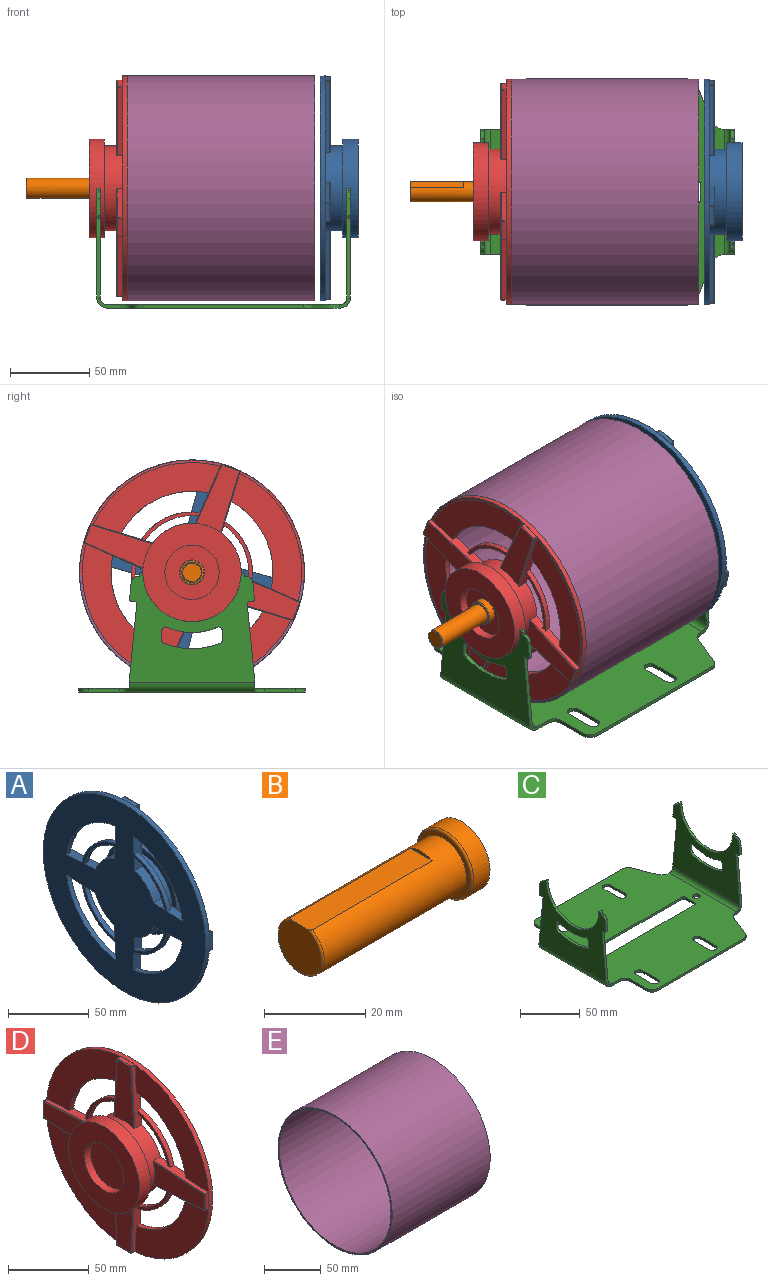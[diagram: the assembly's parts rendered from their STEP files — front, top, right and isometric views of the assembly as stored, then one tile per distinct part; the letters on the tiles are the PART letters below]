
ASSEMBLY  parts=5 mates=4
PART A: 69 faces, bbox 24x142.2x142.2 mm
  f0: plane 34.29x34.29mm, normal (1,0,0), area 923.5mm2, adj f5
  f1: cylinder r=26.92mm len=53.85mm, axis (1,0,0), area 1960.8mm2, adj f2,f6,f7,f8,f9,f10,f11,f12
  f2: plane 62.23x62.23mm, normal (-1,0,0), area 764.2mm2, adj f1,f3
  f3: cylinder r=31.12mm len=62.23mm, axis (1,0,0), area 1862.1mm2, adj f2,f4
  f4: plane 62.23x62.23mm, normal (1,0,0), area 2118mm2, adj f3,f5
  f5: cylinder r=17.14mm len=34.29mm, axis (1,0,0), area 574.6mm2, adj f0,f4
  f6: plane 142.24x142.24mm, normal (-1,0,0), area 11924.2mm2, adj f1,f15,f16,f17,f19,f20,f33,f34
  f7: cylinder r=0.51mm len=45.04mm, axis (0,0.06,1), area 35.9mm2, adj f1,f33,f53,f54
  f8: cylinder r=0.51mm len=45.04mm, axis (0,0.06,-1), area 35.9mm2, adj f1,f34,f53,f56
  f9: cylinder r=0.51mm len=45.04mm, axis (0,-1,0.06), area 35.9mm2, adj f1,f35,f57,f58
  f10: cylinder r=0.51mm len=45.04mm, axis (0,1,0.06), area 35.9mm2, adj f1,f36,f57,f60
  f11: cylinder r=0.51mm len=45.04mm, axis (0,-0.06,-1), area 35.9mm2, adj f1,f37,f61,f62
  f12: cylinder r=0.51mm len=45.04mm, axis (0,-0.06,1), area 35.9mm2, adj f1,f38,f61,f64
  f13: cylinder r=0.51mm len=45.04mm, axis (0,1,-0.06), area 35.9mm2, adj f1,f39,f65,f66
  f14: cylinder r=0.51mm len=45.04mm, axis (0,-1,-0.06), area 35.9mm2, adj f1,f40,f65,f68
  f15: cylinder r=51.26mm len=43.12mm, axis (1,0,0), area 215.7mm2, adj f6,f18,f33,f36
  f16: cylinder r=51.26mm len=43.12mm, axis (1,0,0), area 215.7mm2, adj f6,f18,f35,f38
  f17: cylinder r=51.26mm len=43.12mm, axis (1,0,0), area 215.7mm2, adj f6,f18,f37,f40
  f18: plane 142.24x142.24mm, normal (1,0,0), area 6535.9mm2, adj f15,f16,f17,f19,f20,f21,f22,f23
  f19: cylinder r=71.12mm len=142.24mm, axis (1,0,0), area 1475.5mm2, adj f6,f18
  f20: cylinder r=51.26mm len=43.12mm, axis (1,0,0), area 215.7mm2, adj f6,f18,f34,f39
  f21: plane 11.8x2.79mm, normal (0,0,1), area 33mm2, adj f18,f22,f23,f55
  f22: cylinder r=0.51mm len=2.79mm, axis (-1,0,0), area 2.1mm2, adj f18,f21,f33,f54
  f23: cylinder r=0.51mm len=2.79mm, axis (-1,0,0), area 2.1mm2, adj f18,f21,f34,f56
  f24: plane 11.8x2.79mm, normal (0,-1,0), area 33mm2, adj f18,f25,f26,f59
  f25: cylinder r=0.51mm len=2.79mm, axis (-1,0,0), area 2.1mm2, adj f18,f24,f35,f58
  f26: cylinder r=0.51mm len=2.79mm, axis (-1,0,0), area 2.1mm2, adj f18,f24,f36,f60
  f27: plane 11.8x2.79mm, normal (0,0,-1), area 33mm2, adj f18,f28,f29,f63
  f28: cylinder r=0.51mm len=2.79mm, axis (-1,0,0), area 2.1mm2, adj f18,f27,f37,f62
  f29: cylinder r=0.51mm len=2.79mm, axis (-1,0,0), area 2.1mm2, adj f18,f27,f38,f64
  f30: plane 11.8x2.79mm, normal (0,1,0), area 33mm2, adj f18,f31,f32,f67
  f31: cylinder r=0.51mm len=2.79mm, axis (-1,0,0), area 2.1mm2, adj f18,f30,f39,f66
  f32: cylinder r=0.51mm len=2.79mm, axis (-1,0,0), area 2.1mm2, adj f18,f30,f40,f68
  f33: plane 45.01x6.1mm, normal (0,-1,0.06), area 201.9mm2, adj f1,f6,f7,f15,f18,f22,f50,f51
  f34: plane 45.01x6.1mm, normal (0,1,0.06), area 201.9mm2, adj f1,f6,f8,f18,f20,f23,f41,f42
  f35: plane 45.01x6.1mm, normal (0,-0.06,-1), area 201.9mm2, adj f1,f6,f9,f16,f18,f25,f47,f48
  f36: plane 45.01x6.1mm, normal (0,-0.06,1), area 201.9mm2, adj f1,f6,f10,f15,f18,f26,f50,f51
  f37: plane 45.01x6.1mm, normal (0,1,-0.06), area 201.9mm2, adj f1,f6,f11,f17,f18,f28,f44,f45
  f38: plane 45.01x6.1mm, normal (0,-1,-0.06), area 201.9mm2, adj f1,f6,f12,f16,f18,f29,f47,f48
  f39: plane 45.01x6.1mm, normal (0,0.06,1), area 201.9mm2, adj f1,f6,f13,f18,f20,f31,f41,f42
  f40: plane 45.01x6.1mm, normal (0,0.06,-1), area 201.9mm2, adj f1,f6,f14,f17,f18,f32,f44,f45
  f41: cylinder r=38.23mm len=28.94mm, axis (1,0,0), area 142.6mm2, adj f6,f34,f39,f43
  f42: cylinder r=35.94mm len=26.42mm, axis (1,0,0), area 129.7mm2, adj f6,f34,f39,f43
  f43: plane 28.94x28.94mm, normal (1,0,0), area 94.3mm2, adj f34,f39,f41,f42
  f44: cylinder r=38.23mm len=28.94mm, axis (1,0,0), area 142.6mm2, adj f6,f37,f40,f46
  f45: cylinder r=35.94mm len=26.42mm, axis (1,0,0), area 129.7mm2, adj f6,f37,f40,f46
  f46: plane 28.94x28.94mm, normal (1,0,0), area 94.3mm2, adj f37,f40,f44,f45
  f47: cylinder r=38.23mm len=28.94mm, axis (1,0,0), area 142.6mm2, adj f6,f35,f38,f49
  f48: cylinder r=35.94mm len=26.42mm, axis (1,0,0), area 129.7mm2, adj f6,f35,f38,f49
  f49: plane 28.94x28.94mm, normal (1,0,0), area 94.3mm2, adj f35,f38,f47,f48
  f50: cylinder r=38.23mm len=28.94mm, axis (1,0,0), area 142.6mm2, adj f6,f33,f36,f52
  f51: cylinder r=35.94mm len=26.42mm, axis (1,0,0), area 129.7mm2, adj f6,f33,f36,f52
  f52: plane 28.94x28.94mm, normal (1,0,0), area 94.3mm2, adj f33,f36,f50,f51
  f53: plane 44.8x17.1mm, normal (1,0,0), area 631.4mm2, adj f1,f7,f8,f55
  f54: sphere r=0.51mm, area 0.4mm2, adj f7,f22,f55
  f55: cylinder r=0.51mm len=11.8mm, axis (0,1,0), area 9.4mm2, adj f21,f53,f54,f56
  f56: sphere r=0.51mm, area 0.4mm2, adj f8,f23,f55
  f57: plane 44.8x17.1mm, normal (1,0,0), area 631.4mm2, adj f1,f9,f10,f59
  f58: sphere r=0.51mm, area 0.4mm2, adj f9,f25,f59
  f59: cylinder r=0.51mm len=11.8mm, axis (0,0,1), area 9.4mm2, adj f24,f57,f58,f60
  f60: sphere r=0.51mm, area 0.4mm2, adj f10,f26,f59
  f61: plane 44.8x17.1mm, normal (1,0,0), area 631.4mm2, adj f1,f11,f12,f63
  f62: sphere r=0.51mm, area 0.4mm2, adj f11,f28,f63
  f63: cylinder r=0.51mm len=11.8mm, axis (0,-1,0), area 9.4mm2, adj f27,f61,f62,f64
  f64: sphere r=0.51mm, area 0.4mm2, adj f12,f29,f63
  f65: plane 44.8x17.1mm, normal (1,0,0), area 631.4mm2, adj f1,f13,f14,f67
  f66: sphere r=0.51mm, area 0.4mm2, adj f13,f31,f67
  f67: cylinder r=0.51mm len=11.8mm, axis (0,0,-1), area 9.4mm2, adj f30,f65,f66,f68
  f68: sphere r=0.51mm, area 0.4mm2, adj f14,f32,f67
PART B: 9 faces, bbox 45.4x17.1x17.1 mm
  f0: plane 11.68x11.43mm, normal (-1,0,0), area 106.6mm2, adj f5,f7
  f1: cylinder r=7.89mm len=15.77mm, axis (1,0,0), area 226.6mm2, adj f2,f6
  f2: torus R=7.38mm, axis (1,0,0), area 38.6mm2, adj f1,f3
  f3: plane 14.76x14.76mm, normal (-1,0,0), area 44.4mm2, adj f2,f4
  f4: cylinder r=6.35mm len=39.78mm, axis (1,0,0), area 1376.3mm2, adj f3,f5,f7,f8
  f5: torus R=5.84mm, axis (1,0,0), area 26.7mm2, adj f0,f4,f7
  f6: plane 15.77x15.77mm, normal (1,0,0), area 195.4mm2, adj f1
  f7: plane 34.04x6.03mm, normal (0,0,1), area 205.1mm2, adj f0,f4,f5,f8
  f8: plane 6.03x0.76mm, normal (-1,0,0), area 3.1mm2, adj f4,f7
PART C: 108 faces, bbox 160.4x143x75.7 mm
  f0: plane 147.7x143mm, normal (0,0,-1), area 16724.9mm2, adj f2,f3,f12,f13,f14,f15,f18,f19
  f1: plane 147.7x143mm, normal (0,0,1), area 16724.9mm2, adj f2,f3,f12,f13,f16,f17,f18,f19
  f2: plane 6.64x6.35mm, normal (0,-1,0), area 19.4mm2, adj f0,f1,f15,f16,f45,f57
  f3: plane 6.64x6.35mm, normal (0,1,0), area 19.4mm2, adj f0,f1,f15,f16,f31,f72
  f4: plane 79.5x69.34mm, normal (1,0,0), area 3277.4mm2, adj f5,f6,f17,f73,f74,f75,f76,f77
  f5: plane 2.29x0.75mm, normal (0,0,1), area 1.7mm2, adj f4,f7,f96,f97
  f6: plane 2.29x0.75mm, normal (0,0,1), area 1.7mm2, adj f4,f7,f81,f97
  f7: plane 79.5x69.34mm, normal (-1,0,0), area 3277.4mm2, adj f5,f6,f14,f73,f74,f75,f76,f77
  f8: plane 79.5x69.34mm, normal (1,0,0), area 3277.4mm2, adj f9,f10,f15,f48,f49,f50,f51,f52
  f9: plane 2.29x0.75mm, normal (0,0,1), area 1.7mm2, adj f8,f11,f48,f65
  f10: plane 2.29x0.75mm, normal (0,0,1), area 1.7mm2, adj f8,f11,f48,f64
  f11: plane 79.5x69.34mm, normal (-1,0,0), area 3277.4mm2, adj f9,f10,f16,f48,f49,f50,f51,f52
  f12: plane 15.88x6.35mm, normal (0,-1,0), area 40.5mm2, adj f0,f1,f14,f17,f39,f88
  f13: plane 15.88x6.35mm, normal (0,1,0), area 40.5mm2, adj f0,f1,f14,f17,f32,f89
  f14: cylinder r=6.35mm len=79.5mm, axis (0,1,0), area 793mm2, adj f0,f7,f12,f13
  f15: cylinder r=6.35mm len=79.5mm, axis (0,1,0), area 793mm2, adj f0,f2,f3,f8
  f16: cylinder r=4.06mm len=79.5mm, axis (0,1,0), area 507.5mm2, adj f1,f2,f3,f11
  f17: cylinder r=4.06mm len=79.5mm, axis (0,1,0), area 507.5mm2, adj f1,f4,f12,f13
  f18: plane 22.07x8.65mm, normal (0.93,0.36,0), area 54.2mm2, adj f0,f1,f19,f31
  f19: cylinder r=6.35mm len=5.91mm, axis (0,0,-1), area 17.4mm2, adj f0,f1,f18,f20
  f20: plane 102.35x2.29mm, normal (0,1,0), area 234mm2, adj f0,f1,f19,f21
  f21: cylinder r=6.35mm len=6.35mm, axis (0,0,-1), area 22.8mm2, adj f0,f1,f20,f22
  f22: plane 19.05x2.29mm, normal (-1,0,0), area 43.5mm2, adj f0,f1,f21,f32
  f23: cylinder r=3.97mm len=7.94mm, axis (0,0,-1), area 28.5mm2, adj f0,f1,f24,f26
  f24: plane 17.46x2.29mm, normal (-1,0,0), area 39.9mm2, adj f0,f1,f23,f25
  f25: cylinder r=3.97mm len=7.94mm, axis (0,0,-1), area 28.5mm2, adj f0,f1,f24,f26
  f26: plane 17.46x2.29mm, normal (1,0,0), area 39.9mm2, adj f0,f1,f23,f25
  f27: plane 17.46x2.29mm, normal (1,0,0), area 39.9mm2, adj f0,f1,f28,f30
  f28: cylinder r=3.97mm len=7.94mm, axis (0,0,-1), area 28.5mm2, adj f0,f1,f27,f29
  f29: plane 17.46x2.29mm, normal (-1,0,0), area 39.9mm2, adj f0,f1,f28,f30
  f30: cylinder r=3.97mm len=7.94mm, axis (0,0,-1), area 28.5mm2, adj f0,f1,f27,f29
  f31: cylinder r=8.89mm len=8.28mm, axis (0,0,-1), area 24.3mm2, adj f0,f1,f3,f18
  f32: cylinder r=6.35mm len=6.35mm, axis (0,0,-1), area 22.8mm2, adj f0,f1,f13,f22
  f33: cylinder r=3.97mm len=7.94mm, axis (0,0,-1), area 28.5mm2, adj f0,f1,f34,f47
  f34: plane 17.46x2.29mm, normal (1,0,0), area 39.9mm2, adj f0,f1,f33,f35
  f35: cylinder r=3.97mm len=7.94mm, axis (0,0,-1), area 28.5mm2, adj f0,f1,f34,f47
  f36: cylinder r=3.97mm len=7.94mm, axis (0,0,-1), area 28.5mm2, adj f0,f1,f37,f46
  f37: plane 17.46x2.29mm, normal (1,0,0), area 39.9mm2, adj f0,f1,f36,f38
  f38: cylinder r=3.97mm len=7.94mm, axis (0,0,-1), area 28.5mm2, adj f0,f1,f37,f46
  f39: cylinder r=6.35mm len=6.35mm, axis (0,0,-1), area 22.8mm2, adj f0,f1,f12,f40
  f40: plane 19.05x2.29mm, normal (-1,0,0), area 43.5mm2, adj f0,f1,f39,f41
  f41: cylinder r=6.35mm len=6.35mm, axis (0,0,-1), area 22.8mm2, adj f0,f1,f40,f42
  f42: plane 102.35x2.29mm, normal (0,-1,0), area 234mm2, adj f0,f1,f41,f43
  f43: cylinder r=6.35mm len=5.91mm, axis (0,0,-1), area 17.4mm2, adj f0,f1,f42,f44
  f44: plane 22.07x8.65mm, normal (0.93,-0.36,0), area 54.2mm2, adj f0,f1,f43,f45
  f45: cylinder r=8.89mm len=8.28mm, axis (0,0,-1), area 24.3mm2, adj f0,f1,f2,f44
  f46: plane 17.46x2.29mm, normal (-1,0,0), area 39.9mm2, adj f0,f1,f36,f38
  f47: plane 17.46x2.29mm, normal (-1,0,0), area 39.9mm2, adj f0,f1,f33,f35
  f48: cylinder r=31.12mm len=62.23mm, axis (-1,0,0), area 223.5mm2, adj f8,f9,f10,f11
  f49: plane 5.51x2.29mm, normal (0,-1,0), area 12.6mm2, adj f8,f11,f50,f56
  f50: cylinder r=2.54mm len=3.58mm, axis (-1,0,0), area 11.6mm2, adj f8,f11,f49,f51
  f51: cylinder r=38.1mm len=31.22mm, axis (-1,0,0), area 73.5mm2, adj f8,f11,f50,f52
  f52: cylinder r=2.54mm len=3.58mm, axis (-1,0,0), area 11.6mm2, adj f8,f11,f51,f53
  f53: plane 5.51x2.29mm, normal (0,1,0), area 12.6mm2, adj f8,f11,f52,f54
  f54: cylinder r=2.54mm len=2.37mm, axis (-1,0,0), area 7mm2, adj f8,f11,f53,f55
  f55: cylinder r=48.26mm len=35.15mm, axis (-1,0,0), area 82.2mm2, adj f8,f11,f54,f56
  f56: cylinder r=2.54mm len=2.37mm, axis (-1,0,0), area 7mm2, adj f8,f11,f49,f55
  f57: plane 50.56x4.91mm, normal (0,-1,0.1), area 116.1mm2, adj f2,f8,f11,f58
  f58: plane 3.54x2.29mm, normal (0,-0.1,-1), area 8.1mm2, adj f8,f11,f57,f59
  f59: cylinder r=1.27mm len=2.29mm, axis (-1,0,0), area 4.6mm2, adj f8,f11,f58,f60
  f60: plane 10.62x2.29mm, normal (0,-1,0.1), area 24.4mm2, adj f8,f11,f59,f61
  f61: cylinder r=4.32mm len=4.72mm, axis (-1,0,0), area 15.5mm2, adj f8,f11,f60,f62
  f62: plane 2.29x0.51mm, normal (0,0.1,1), area 1.2mm2, adj f8,f11,f61,f63
  f63: plane 2.29x1.45mm, normal (0,-1,0.1), area 3.3mm2, adj f8,f11,f62,f64
  f64: cylinder r=1.27mm len=2.29mm, axis (-1,0,0), area 4.3mm2, adj f8,f10,f11,f63
  f65: cylinder r=1.27mm len=2.29mm, axis (-1,0,0), area 4.3mm2, adj f8,f9,f11,f66
  f66: plane 2.29x1.45mm, normal (0,1,0.1), area 3.3mm2, adj f8,f11,f65,f67
  f67: plane 2.29x0.51mm, normal (0,-0.1,1), area 1.2mm2, adj f8,f11,f66,f68
  f68: cylinder r=4.32mm len=4.72mm, axis (-1,0,0), area 15.5mm2, adj f8,f11,f67,f69
  f69: plane 10.62x2.29mm, normal (0,1,0.1), area 24.4mm2, adj f8,f11,f68,f70
  f70: cylinder r=1.27mm len=2.29mm, axis (-1,0,0), area 4.6mm2, adj f8,f11,f69,f71
  f71: plane 3.54x2.29mm, normal (0,0.1,-1), area 8.1mm2, adj f8,f11,f70,f72
  f72: plane 50.56x4.91mm, normal (0,1,0.1), area 116.1mm2, adj f3,f8,f11,f71
  f73: cylinder r=2.54mm len=2.37mm, axis (-1,0,0), area 7mm2, adj f4,f7,f74,f80
  f74: cylinder r=48.26mm len=35.15mm, axis (-1,0,0), area 82.2mm2, adj f4,f7,f73,f75
  f75: cylinder r=2.54mm len=2.37mm, axis (-1,0,0), area 7mm2, adj f4,f7,f74,f76
  f76: plane 5.51x2.29mm, normal (0,1,0), area 12.6mm2, adj f4,f7,f75,f77
  f77: cylinder r=2.54mm len=3.58mm, axis (-1,0,0), area 11.6mm2, adj f4,f7,f76,f78
  f78: cylinder r=38.1mm len=31.22mm, axis (-1,0,0), area 73.5mm2, adj f4,f7,f77,f79
  f79: cylinder r=2.54mm len=3.58mm, axis (-1,0,0), area 11.6mm2, adj f4,f7,f78,f80
  f80: plane 5.51x2.29mm, normal (0,-1,0), area 12.6mm2, adj f4,f7,f73,f79
  f81: cylinder r=1.27mm len=2.29mm, axis (-1,0,0), area 4.3mm2, adj f4,f6,f7,f82
  f82: plane 2.29x1.45mm, normal (0,-1,0.1), area 3.3mm2, adj f4,f7,f81,f83
  f83: plane 2.29x0.51mm, normal (0,0.1,1), area 1.2mm2, adj f4,f7,f82,f84
  f84: cylinder r=4.32mm len=4.72mm, axis (-1,0,0), area 15.5mm2, adj f4,f7,f83,f85
  f85: plane 10.62x2.29mm, normal (0,-1,0.1), area 24.4mm2, adj f4,f7,f84,f86
  f86: cylinder r=1.27mm len=2.29mm, axis (-1,0,0), area 4.6mm2, adj f4,f7,f85,f87
  f87: plane 3.54x2.29mm, normal (0,-0.1,-1), area 8.1mm2, adj f4,f7,f86,f88
  f88: plane 50.56x4.91mm, normal (0,-1,0.1), area 116.1mm2, adj f4,f7,f12,f87
  f89: plane 50.56x4.91mm, normal (0,1,0.1), area 116.1mm2, adj f4,f7,f13,f90
  f90: plane 3.54x2.29mm, normal (0,0.1,-1), area 8.1mm2, adj f4,f7,f89,f91
  f91: cylinder r=1.27mm len=2.29mm, axis (-1,0,0), area 4.6mm2, adj f4,f7,f90,f92
  f92: plane 10.62x2.29mm, normal (0,1,0.1), area 24.4mm2, adj f4,f7,f91,f93
  f93: cylinder r=4.32mm len=4.72mm, axis (-1,0,0), area 15.5mm2, adj f4,f7,f92,f94
  f94: plane 2.29x0.51mm, normal (0,-0.1,1), area 1.2mm2, adj f4,f7,f93,f95
  f95: plane 2.29x1.45mm, normal (0,1,0.1), area 3.3mm2, adj f4,f7,f94,f96
  f96: cylinder r=1.27mm len=2.29mm, axis (-1,0,0), area 4.3mm2, adj f4,f5,f7,f95
  f97: cylinder r=31.12mm len=62.23mm, axis (-1,0,0), area 223.5mm2, adj f4,f5,f6,f7
  f98: cylinder r=2.54mm len=2.54mm, axis (0,0,1), area 9.1mm2, adj f0,f1,f99,f105
  f99: plane 112.14x2.29mm, normal (0,1,0), area 256.4mm2, adj f0,f1,f98,f100
  f100: cylinder r=2.54mm len=2.54mm, axis (0,0,1), area 9.1mm2, adj f0,f1,f99,f101
  f101: plane 10.16x2.29mm, normal (-1,0,0), area 23.2mm2, adj f0,f1,f100,f102
  f102: cylinder r=2.54mm len=2.54mm, axis (0,0,1), area 9.1mm2, adj f0,f1,f101,f103
  f103: plane 112.14x2.29mm, normal (0,-1,0), area 256.4mm2, adj f0,f1,f102,f104
  f104: cylinder r=2.54mm len=2.54mm, axis (0,0,1), area 9.1mm2, adj f0,f1,f103,f105
  f105: plane 10.16x2.29mm, normal (1,0,0), area 23.2mm2, adj f0,f1,f98,f104
  f106: cylinder r=3.17mm len=6.35mm, axis (0,0,1), area 45.6mm2, adj f0,f1
  f107: cylinder r=3.17mm len=6.35mm, axis (0,0,1), area 45.6mm2, adj f0,f1
PART D: 69 faces, bbox 24x142.2x142.2 mm
  f0: plane 34.29x34.29mm, normal (-1,0,0), area 923.5mm2, adj f5
  f1: cylinder r=26.92mm len=53.85mm, axis (-1,0,0), area 1960.8mm2, adj f2,f6,f7,f8,f9,f10,f11,f12
  f2: plane 62.23x62.23mm, normal (1,0,0), area 764.2mm2, adj f1,f3
  f3: cylinder r=31.12mm len=62.23mm, axis (-1,0,0), area 1862.1mm2, adj f2,f4
  f4: plane 62.23x62.23mm, normal (-1,0,0), area 2118mm2, adj f3,f5
  f5: cylinder r=17.14mm len=34.29mm, axis (-1,0,0), area 574.6mm2, adj f0,f4
  f6: plane 142.24x142.24mm, normal (1,0,0), area 11924.2mm2, adj f1,f15,f16,f17,f19,f20,f33,f34
  f7: cylinder r=0.51mm len=45.04mm, axis (0,0.06,1), area 35.9mm2, adj f1,f33,f53,f54
  f8: cylinder r=0.51mm len=45.04mm, axis (0,0.06,-1), area 35.9mm2, adj f1,f34,f53,f56
  f9: cylinder r=0.51mm len=45.04mm, axis (0,-1,0.06), area 35.9mm2, adj f1,f35,f57,f58
  f10: cylinder r=0.51mm len=45.04mm, axis (0,1,0.06), area 35.9mm2, adj f1,f36,f57,f60
  f11: cylinder r=0.51mm len=45.04mm, axis (0,-0.06,-1), area 35.9mm2, adj f1,f37,f61,f62
  f12: cylinder r=0.51mm len=45.04mm, axis (0,-0.06,1), area 35.9mm2, adj f1,f38,f61,f64
  f13: cylinder r=0.51mm len=45.04mm, axis (0,1,-0.06), area 35.9mm2, adj f1,f39,f65,f66
  f14: cylinder r=0.51mm len=45.04mm, axis (0,-1,-0.06), area 35.9mm2, adj f1,f40,f65,f68
  f15: cylinder r=51.26mm len=43.12mm, axis (-1,0,0), area 215.7mm2, adj f6,f18,f33,f36
  f16: cylinder r=51.26mm len=43.12mm, axis (-1,0,0), area 215.7mm2, adj f6,f18,f35,f38
  f17: cylinder r=51.26mm len=43.12mm, axis (-1,0,0), area 215.7mm2, adj f6,f18,f37,f40
  f18: plane 142.24x142.24mm, normal (-1,0,0), area 6535.9mm2, adj f15,f16,f17,f19,f20,f21,f22,f23
  f19: cylinder r=71.12mm len=142.24mm, axis (-1,0,0), area 1475.5mm2, adj f6,f18
  f20: cylinder r=51.26mm len=43.12mm, axis (-1,0,0), area 215.7mm2, adj f6,f18,f34,f39
  f21: plane 11.8x2.79mm, normal (0,0,1), area 33mm2, adj f18,f22,f23,f55
  f22: cylinder r=0.51mm len=2.79mm, axis (1,0,0), area 2.1mm2, adj f18,f21,f33,f54
  f23: cylinder r=0.51mm len=2.79mm, axis (1,0,0), area 2.1mm2, adj f18,f21,f34,f56
  f24: plane 11.8x2.79mm, normal (0,-1,0), area 33mm2, adj f18,f25,f26,f59
  f25: cylinder r=0.51mm len=2.79mm, axis (1,0,0), area 2.1mm2, adj f18,f24,f35,f58
  f26: cylinder r=0.51mm len=2.79mm, axis (1,0,0), area 2.1mm2, adj f18,f24,f36,f60
  f27: plane 11.8x2.79mm, normal (0,0,-1), area 33mm2, adj f18,f28,f29,f63
  f28: cylinder r=0.51mm len=2.79mm, axis (1,0,0), area 2.1mm2, adj f18,f27,f37,f62
  f29: cylinder r=0.51mm len=2.79mm, axis (1,0,0), area 2.1mm2, adj f18,f27,f38,f64
  f30: plane 11.8x2.79mm, normal (0,1,0), area 33mm2, adj f18,f31,f32,f67
  f31: cylinder r=0.51mm len=2.79mm, axis (1,0,0), area 2.1mm2, adj f18,f30,f39,f66
  f32: cylinder r=0.51mm len=2.79mm, axis (1,0,0), area 2.1mm2, adj f18,f30,f40,f68
  f33: plane 45.01x6.1mm, normal (0,-1,0.06), area 201.9mm2, adj f1,f6,f7,f15,f18,f22,f50,f51
  f34: plane 45.01x6.1mm, normal (0,1,0.06), area 201.9mm2, adj f1,f6,f8,f18,f20,f23,f41,f42
  f35: plane 45.01x6.1mm, normal (0,-0.06,-1), area 201.9mm2, adj f1,f6,f9,f16,f18,f25,f47,f48
  f36: plane 45.01x6.1mm, normal (0,-0.06,1), area 201.9mm2, adj f1,f6,f10,f15,f18,f26,f50,f51
  f37: plane 45.01x6.1mm, normal (0,1,-0.06), area 201.9mm2, adj f1,f6,f11,f17,f18,f28,f44,f45
  f38: plane 45.01x6.1mm, normal (0,-1,-0.06), area 201.9mm2, adj f1,f6,f12,f16,f18,f29,f47,f48
  f39: plane 45.01x6.1mm, normal (0,0.06,1), area 201.9mm2, adj f1,f6,f13,f18,f20,f31,f41,f42
  f40: plane 45.01x6.1mm, normal (0,0.06,-1), area 201.9mm2, adj f1,f6,f14,f17,f18,f32,f44,f45
  f41: cylinder r=38.23mm len=28.94mm, axis (-1,0,0), area 142.6mm2, adj f6,f34,f39,f43
  f42: cylinder r=35.94mm len=26.42mm, axis (-1,0,0), area 129.7mm2, adj f6,f34,f39,f43
  f43: plane 28.94x28.94mm, normal (-1,0,0), area 94.3mm2, adj f34,f39,f41,f42
  f44: cylinder r=38.23mm len=28.94mm, axis (-1,0,0), area 142.6mm2, adj f6,f37,f40,f46
  f45: cylinder r=35.94mm len=26.42mm, axis (-1,0,0), area 129.7mm2, adj f6,f37,f40,f46
  f46: plane 28.94x28.94mm, normal (-1,0,0), area 94.3mm2, adj f37,f40,f44,f45
  f47: cylinder r=38.23mm len=28.94mm, axis (-1,0,0), area 142.6mm2, adj f6,f35,f38,f49
  f48: cylinder r=35.94mm len=26.42mm, axis (-1,0,0), area 129.7mm2, adj f6,f35,f38,f49
  f49: plane 28.94x28.94mm, normal (-1,0,0), area 94.3mm2, adj f35,f38,f47,f48
  f50: cylinder r=38.23mm len=28.94mm, axis (-1,0,0), area 142.6mm2, adj f6,f33,f36,f52
  f51: cylinder r=35.94mm len=26.42mm, axis (-1,0,0), area 129.7mm2, adj f6,f33,f36,f52
  f52: plane 28.94x28.94mm, normal (-1,0,0), area 94.3mm2, adj f33,f36,f50,f51
  f53: plane 44.8x17.1mm, normal (-1,0,0), area 631.4mm2, adj f1,f7,f8,f55
  f54: sphere r=0.51mm, area 0.4mm2, adj f7,f22,f55
  f55: cylinder r=0.51mm len=11.8mm, axis (0,1,0), area 9.4mm2, adj f21,f53,f54,f56
  f56: sphere r=0.51mm, area 0.4mm2, adj f8,f23,f55
  f57: plane 44.8x17.1mm, normal (-1,0,0), area 631.4mm2, adj f1,f9,f10,f59
  f58: sphere r=0.51mm, area 0.4mm2, adj f9,f25,f59
  f59: cylinder r=0.51mm len=11.8mm, axis (0,0,1), area 9.4mm2, adj f24,f57,f58,f60
  f60: sphere r=0.51mm, area 0.4mm2, adj f10,f26,f59
  f61: plane 44.8x17.1mm, normal (-1,0,0), area 631.4mm2, adj f1,f11,f12,f63
  f62: sphere r=0.51mm, area 0.4mm2, adj f11,f28,f63
  f63: cylinder r=0.51mm len=11.8mm, axis (0,-1,0), area 9.4mm2, adj f27,f61,f62,f64
  f64: sphere r=0.51mm, area 0.4mm2, adj f12,f29,f63
  f65: plane 44.8x17.1mm, normal (-1,0,0), area 631.4mm2, adj f1,f13,f14,f67
  f66: sphere r=0.51mm, area 0.4mm2, adj f13,f31,f67
  f67: cylinder r=0.51mm len=11.8mm, axis (0,0,-1), area 9.4mm2, adj f30,f65,f66,f68
  f68: sphere r=0.51mm, area 0.4mm2, adj f14,f32,f67
PART E: 4 faces, bbox 121.9x142.2x142.2 mm
  f0: cylinder r=69.47mm len=138.94mm, axis (-1,0,0), area 53216.4mm2, adj f2,f3
  f1: cylinder r=71.12mm len=142.24mm, axis (-1,0,0), area 54481.2mm2, adj f2,f3
  f2: plane 142.24x142.24mm, normal (1,0,0), area 729.2mm2, adj f0,f1
  f3: plane 142.24x142.24mm, normal (-1,0,0), area 729.2mm2, adj f0,f1
PLACE A rot(axis=(1,0,0),102.2deg) t=(-105.45,-41.38,2.96)mm
PLACE B rot(axis=(-1,0,0),55.7deg) t=(-105.45,-41.38,2.96)mm
PLACE C t=(-105.45,-41.38,2.96)mm fixed
PLACE D rot(axis=(1,0,0),20.4deg) t=(-105.45,-41.38,2.96)mm
PLACE E rot(axis=(1,0,0),68.1deg) t=(-108.75,-41.38,2.96)mm
MATE revolute D.f1 <-> B.f1  axis (-1,0,0) through (-124.12,-41.38,2.96)mm
MATE revolute E.f0 <-> D.f1  axis (-1,0,0) through (-108.75,-41.38,2.96)mm
MATE revolute D.f1 <-> C.f48  axis (-1,0,0) through (-124.69,-41.38,2.96)mm
MATE revolute A.f1 <-> C.f48  axis (1,0,0) through (35.71,-41.38,2.96)mm
